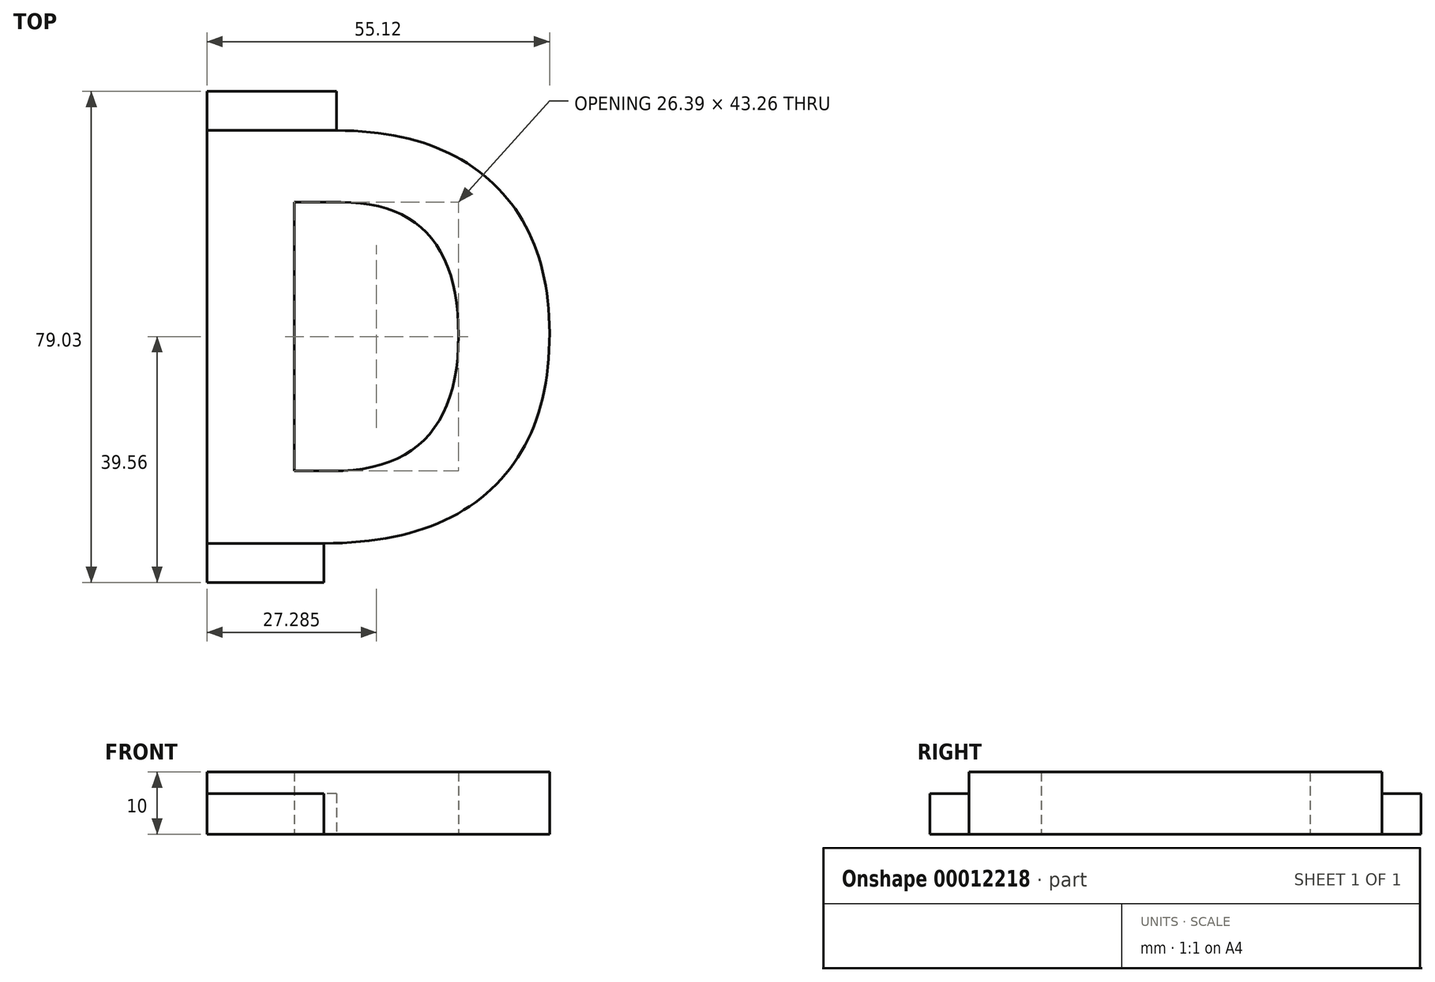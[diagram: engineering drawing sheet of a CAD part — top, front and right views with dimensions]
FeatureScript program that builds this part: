
annotation { "Feature Type Name" : "Feature", "Feature Type Description" : "" }
export const myFeature = defineFeature(function(context is Context, id is Id, definition is map)
    precondition{}
    {
        {
            var Q0;
            Q0=qCreatedBy(makeId("Top.planeOp"),FACE);
            var sketch = newSketch(context, id + "F0", { "sketchPlane" : qUnion([Q0])});
            skText(sketch, "E0", { "text": "D", "fontName": "OpenSans-Bold.ttf"});
            const initialGuessF0  = {"E0": [-0.06348, 0, 1, 0, 0.067]};
            skSetInitialGuess(sketch, initialGuessF0);
            skSolve(sketch);
        }
        {
            var Q0;
            Q0=makeQuery(id+"F0.imprint","IMPRINT",FACE,{"disambiguationData":[TD([[makeQuery(id+"F0.imprint","IMPRINT",EDGE,{"derivedFrom":sQuery(id+"F0.wireOp",EDGE,"E0.sketch_text.stroke-0")}),-1.0]])]});
            extrude(context, id + "F1", {"entities" : qUnion([Q0]), "depth" : 10 * mm});
        }
        {
            var Q0;
            Q0=makeQuery(id+"F1.opExtrude","SWEPT_FACE",FACE,{"disambiguationData":[OSD([sQuery(id+"F0.wireOp",EDGE,"E0.sketch_text.stroke-2")])]});
            var sketch = newSketch(context, id + "F2", { "sketchPlane" : qUnion([Q0])});
            skLineSegment(sketch, "E1.0.0", {"start": v(-55.12, 0) * mm, "end": v(-36.3, 0) * mm});
            skLineSegment(sketch, "E1.0.1", {"start": v(-36.3, 0) * mm, "end": v(-36.3, 10) * mm});
            skLineSegment(sketch, "E1.0.2", {"start": v(-36.3, 10) * mm, "end": v(-55.12, 10) * mm});
            skLineSegment(sketch, "E1.0.3", {"start": v(-55.12, 10) * mm, "end": v(-55.12, 0) * mm});
            skLineSegment(sketch, "E2.top", {"start": v(-55.12, 6.5) * mm, "end": v(-36.3, 6.5) * mm});
            skLineSegment(sketch, "E2.left", {"start": v(-55.12, 0) * mm, "end": v(-55.12, 6.5) * mm});
            skLineSegment(sketch, "E2.right", {"start": v(-36.3, 0) * mm, "end": v(-36.3, 6.5) * mm});
            skSolve(sketch);
        }
        {
            var Q0;
            Q0=makeQuery(id+"F2.imprint","IMPRINT",FACE,{"disambiguationData":[TD([[makeQuery(id+"F2.imprint","IMPRINT",EDGE,{"derivedFrom":sQuery(id+"F2.wireOp",EDGE,"E1.0.0")}),-1.0]])]});
            extrude(context, id + "F3", {"entities" : qUnion([Q0]), "operationType" : NewBodyOperationType.ADD, "depth" : 6.3 * mm});
        }
        {
            var Q0;
            Q0=makeQuery(id+"F1.opExtrude","SWEPT_FACE",FACE,{"disambiguationData":[OSD([sQuery(id+"F0.wireOp",EDGE,"E0.sketch_text.stroke-4")])]});
            var sketch = newSketch(context, id + "F4", { "sketchPlane" : qUnion([Q0])});
            skLineSegment(sketch, "E3.0.0", {"start": v(34.27, 0) * mm, "end": v(55.12, 0) * mm});
            skLineSegment(sketch, "E3.0.1", {"start": v(55.12, 0) * mm, "end": v(55.12, 10) * mm});
            skLineSegment(sketch, "E3.0.2", {"start": v(55.12, 10) * mm, "end": v(34.27, 10) * mm});
            skLineSegment(sketch, "E3.0.3", {"start": v(34.27, 10) * mm, "end": v(34.27, 0) * mm});
            skLineSegment(sketch, "E4.top", {"start": v(34.27, 6.5) * mm, "end": v(55.12, 6.5) * mm});
            skLineSegment(sketch, "E4.left", {"start": v(34.27, 0) * mm, "end": v(34.27, 6.5) * mm});
            skLineSegment(sketch, "E4.right", {"start": v(55.12, 0) * mm, "end": v(55.12, 6.5) * mm});
            skSolve(sketch);
        }
        {
            var Q0;
            Q0=makeQuery(id+"F4.imprint","IMPRINT",FACE,{"disambiguationData":[TD([[makeQuery(id+"F4.imprint","IMPRINT",EDGE,{"derivedFrom":sQuery(id+"F4.wireOp",EDGE,"E3.0.0")}),-1.0]])]});
            extrude(context, id + "F5", {"entities" : qUnion([Q0]), "operationType" : NewBodyOperationType.ADD, "depth" : 6.3 * mm});
        }
    });
